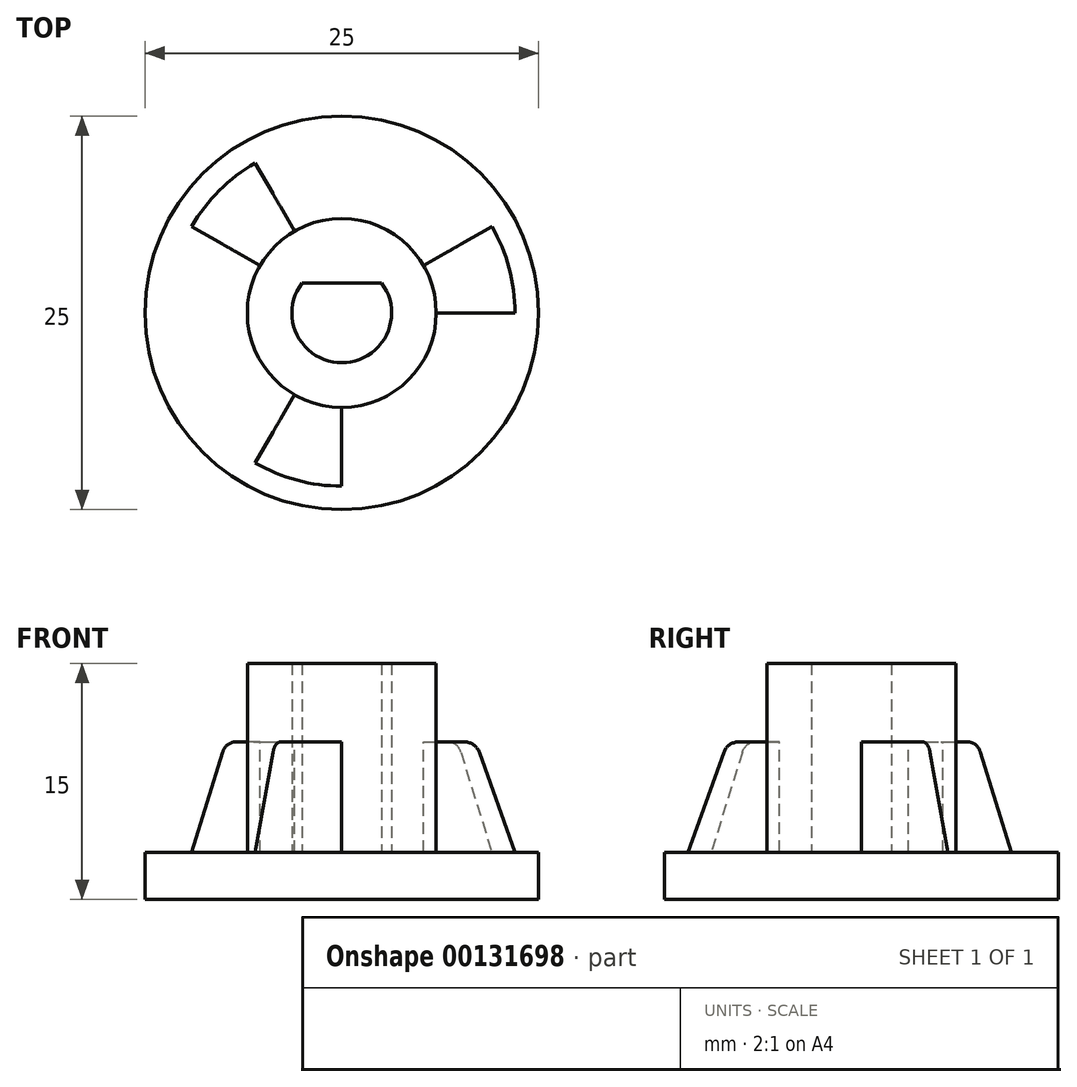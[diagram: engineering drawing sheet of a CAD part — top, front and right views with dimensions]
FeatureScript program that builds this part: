
annotation { "Feature Type Name" : "Feature", "Feature Type Description" : "" }
export const myFeature = defineFeature(function(context is Context, id is Id, definition is map)
    precondition{}
    {
        {
            var Q0;
            Q0=qCreatedBy(makeId("Top.planeOp"),FACE);
            var sketch = newSketch(context, id + "F0", { "sketchPlane" : qUnion([Q0])});
            skArc(sketch, "E0", {"start": v(-2.53, 1.9) * mm, "mid": v(0, -3.17) * mm, "end": v(2.53, 1.9) * mm});
            skLineSegment(sketch, "E1", {"start": v(-2.53, 1.9) * mm, "end": v(2.53, 1.9) * mm});
            skCircle(sketch, "E2", {"center": v(0, 0) * mm, "radius": 6 * mm});
            skLineSegment(sketch, "E3", {"start": v(0, 0) * mm, "end": v(0, -6) * mm, "construction": true});
            skLineSegment(sketch, "E4", {"start": v(0, 0) * mm, "end": v(-5.2, 3) * mm, "construction": true});
            skLineSegment(sketch, "E5", {"start": v(-5.2, 3) * mm, "end": v(5.2, 3) * mm, "construction": true});
            skLineSegment(sketch, "E6", {"start": v(5.2, 3) * mm, "end": v(0, 0) * mm, "construction": true});
            skLineSegment(sketch, "E7", {"start": v(0, 0) * mm, "end": v(0, 3) * mm});
            skLineSegment(sketch, "E8", {"start": v(-6, 0) * mm, "end": v(6, 0) * mm, "construction": true});
            skSolve(sketch);
        }
        {
            var Q0;
            Q0=makeQuery(id+"F0.imprint","IMPRINT",FACE,{"disambiguationData":[TD([[makeQuery(id+"F0.imprint","IMPRINT",EDGE,{"derivedFrom":sQuery(id+"F0.wireOp",EDGE,"E0")}),-1.0]])]});
            extrude(context, id + "F1", {"entities" : qUnion([Q0]), "depth" : 15 * mm});
        }
        {
            var Q0;
            Q0=qCreatedBy(makeId("Top.planeOp"),FACE);
            var sketch = newSketch(context, id + "F2", { "sketchPlane" : qUnion([Q0])});
            skCircle(sketch, "E9", {"center": v(0, 0) * mm, "radius": 12.5 * mm});
            skSolve(sketch);
        }
        {
            var Q0;
            Q0=makeQuery(id+"F2.imprint","IMPRINT",FACE,{"disambiguationData":[TD([[makeQuery(id+"F2.imprint","IMPRINT",EDGE,{"derivedFrom":sQuery(id+"F2.wireOp",EDGE,"E9")}),1.0]])]});
            extrude(context, id + "F3", {"entities" : qUnion([Q0]), "operationType" : NewBodyOperationType.ADD, "depth" : 3 * mm});
        }
        {
            var Q0;
            Q0=qCreatedBy(makeId("Front.planeOp"),FACE);
            var sketch = newSketch(context, id + "F4", { "sketchPlane" : qUnion([Q0])});
            skLineSegment(sketch, "E10", {"start": v(0, 0) * mm, "end": v(0, 10) * mm});
            skLineSegment(sketch, "E11", {"start": v(0, 10) * mm, "end": v(6, 10) * mm});
            skLineSegment(sketch, "E12", {"start": v(6, 0) * mm, "end": v(6, 10) * mm});
            skLineSegment(sketch, "E13", {"start": v(6, 10) * mm, "end": v(7.8, 10) * mm});
            skLineSegment(sketch, "E14", {"start": v(8.74, 9.34) * mm, "end": v(11, 3) * mm});
            skLineSegment(sketch, "E15", {"start": v(11, 3) * mm, "end": v(6, 3) * mm});
            skLineSegment(sketch, "E16", {"start": v(6, 3) * mm, "end": v(6, 10) * mm});
            skPoint(sketch, "E17.visualSharp", {"position": v(8.5, 10) * mm});
            skArc(sketch, "E17.filletArc", {"start": v(8.74, 9.34) * mm, "mid": v(8.37, 9.82) * mm, "end": v(7.8, 10) * mm});
            skSolve(sketch);
        }
        {
            var Q0;
            Q0=makeQuery(id+"F4.imprint","IMPRINT",FACE,{"disambiguationData":[TD([[makeQuery(id+"F4.imprint","IMPRINT",EDGE,{"derivedFrom":sQuery(id+"F4.wireOp",EDGE,"E13")}),-1.0]])]});
            var Q1;
            Q1=makeQuery(id+"F3.boolean.opBoolean","INTERSECT",EDGE,{"derivedFrom":[makeQuery(id+"F1.opExtrude","SWEPT_FACE",FACE,{"disambiguationData":[OSD([sQuery(id+"F0.wireOp",EDGE,"E2")])]}),makeQuery(id+"F3.opExtrude","CAP_FACE",FACE,{"disambiguationData":[OSD([sQuery(id+"F2.wireOp",EDGE,"E9")])],"isStart":false})]});
            revolve(context, id + "F5", {"operationType" : NewBodyOperationType.ADD, "entities" : qUnion([Q0]), "axis" : qUnion([Q1]), "revolveType" : RevolveType.ONE_DIRECTION, "angle" : 30 * degree});
        }
        {
            var Q0;
            Q0=makeQuery(id+"F1.opExtrude","SWEPT_BODY",BODY,{"disambiguationData":[OSD([sQuery(id+"F0.wireOp",EDGE,"E0"),sQuery(id+"F0.wireOp",EDGE,"E1"),sQuery(id+"F0.wireOp",EDGE,"E2")])]});
            var Q1;
            Q1=makeQuery(id+"F5.opRevolve","CAP_FACE",FACE,{"disambiguationData":[OSD([sQuery(id+"F4.wireOp",EDGE,"E13"),sQuery(id+"F4.wireOp",EDGE,"E14"),sQuery(id+"F4.wireOp",EDGE,"E15"),sQuery(id+"F4.wireOp",EDGE,"E16"),sQuery(id+"F4.wireOp",EDGE,"E17.filletArc")])],"isStart":true});
            var Q2;
            Q2=makeQuery(id+"F5.opRevolve","SWEPT_FACE",FACE,{"disambiguationData":[OSD([sQuery(id+"F4.wireOp",EDGE,"E13")])]});
            var Q3;
            Q3=makeQuery(id+"F5.opRevolve","SWEPT_FACE",FACE,{"disambiguationData":[OSD([sQuery(id+"F4.wireOp",EDGE,"E17.filletArc")])]});
            var Q4;
            Q4=makeQuery(id+"F5.opRevolve","SWEPT_FACE",FACE,{"disambiguationData":[OSD([sQuery(id+"F4.wireOp",EDGE,"E14")])]});
            var Q5;
            Q5=makeQuery(id+"F5.opRevolve","CAP_FACE",FACE,{"disambiguationData":[OSD([sQuery(id+"F4.wireOp",EDGE,"E13"),sQuery(id+"F4.wireOp",EDGE,"E14"),sQuery(id+"F4.wireOp",EDGE,"E15"),sQuery(id+"F4.wireOp",EDGE,"E16"),sQuery(id+"F4.wireOp",EDGE,"E17.filletArc")])],"isStart":false});
            var Q6;
            Q6=makeQuery(id+"F3.opExtrude","CAP_EDGE",EDGE,{"disambiguationData":[OSD([sQuery(id+"F2.wireOp",EDGE,"E9")])],"isStart":false});
            circularPattern(context, id + "F6", {"patternType" : PatternType.FACE, "faces" : qUnion([Q1, Q2, Q3, Q4, Q5]), "axis" : qUnion([Q6]), "angle" : 360 * degree, "instanceCount" : 3, "oppositeDirection" : true, "equalSpace" : true});
        }
    });
